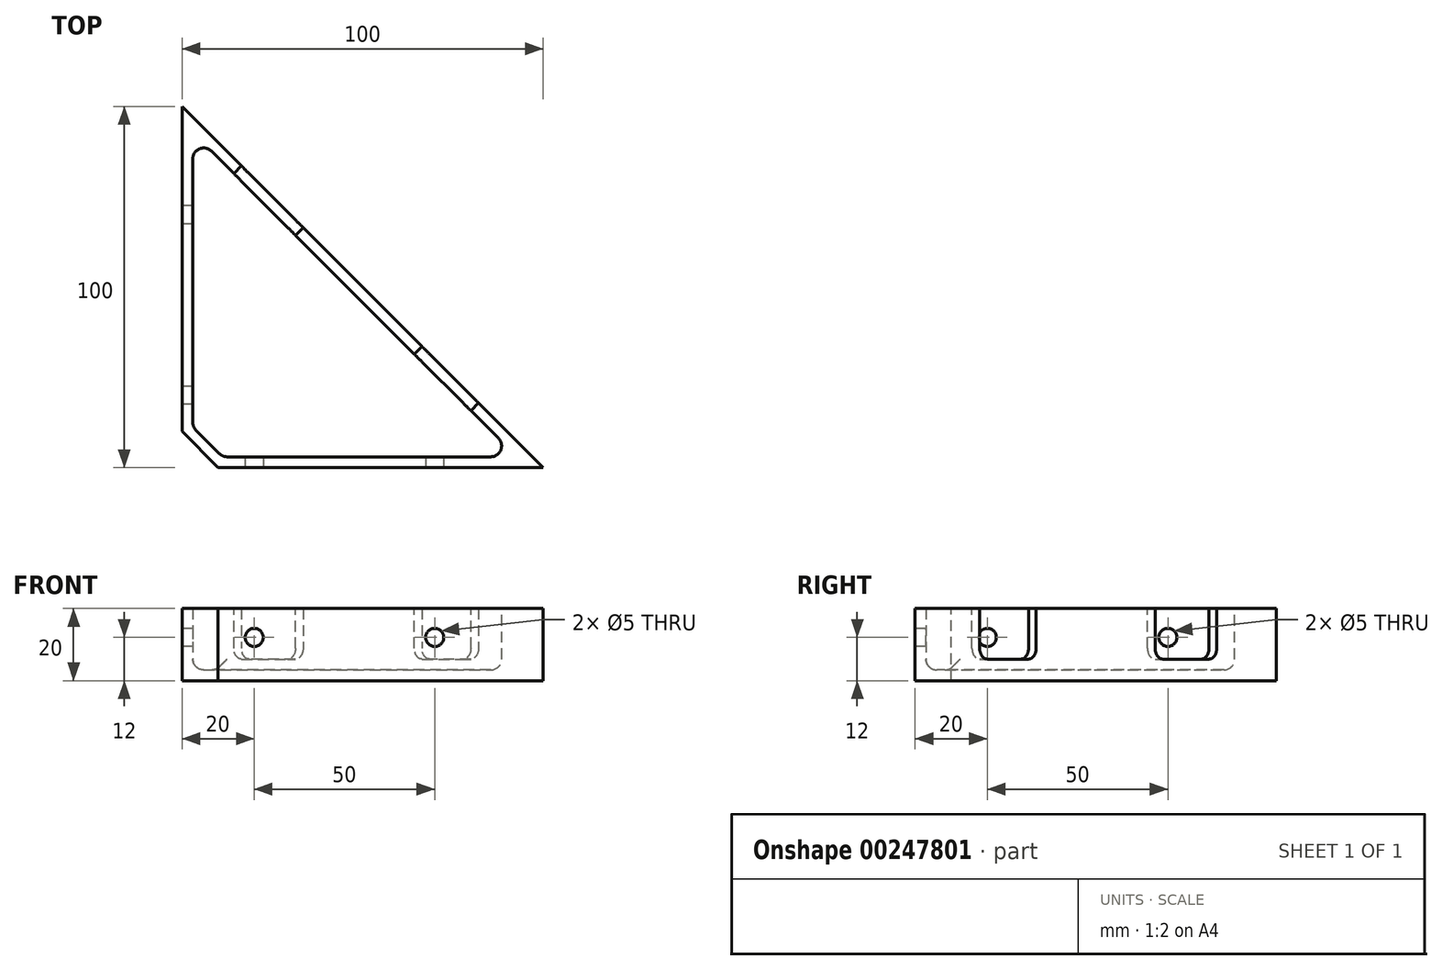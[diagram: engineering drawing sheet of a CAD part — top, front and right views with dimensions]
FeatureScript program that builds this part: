
annotation { "Feature Type Name" : "Feature", "Feature Type Description" : "" }
export const myFeature = defineFeature(function(context is Context, id is Id, definition is map)
    precondition{}
    {
        {
            var Q0;
            Q0=qCreatedBy(makeId("Top.planeOp"),FACE);
            var sketch = newSketch(context, id + "F0", { "sketchPlane" : qUnion([Q0])});
            skLineSegment(sketch, "E0", {"start": v(0, 0) * mm, "end": v(0, 100) * mm});
            skLineSegment(sketch, "E1", {"start": v(0, 100) * mm, "end": v(100, 0) * mm});
            skLineSegment(sketch, "E2", {"start": v(100, 0) * mm, "end": v(0, 0) * mm});
            skLineSegment(sketch, "E3", {"start": v(0, 20) * mm, "end": v(91.8, 20) * mm, "construction": true});
            skLineSegment(sketch, "E4", {"start": v(0, 70) * mm, "end": v(91.8, 70) * mm, "construction": true});
            skLineSegment(sketch, "E5", {"start": v(20, 0) * mm, "end": v(20, 100.49) * mm, "construction": true});
            skLineSegment(sketch, "E6", {"start": v(70, 0) * mm, "end": v(70, 96.45) * mm, "construction": true});
            skSolve(sketch);
        }
        {
            var Q0;
            Q0 = qSketchRegion(id + "F0", true);
            extrude(context, id + "F1", {"entities" : qUnion([Q0]), "depth" : 20 * mm});
        }
        {
            var Q0;
            Q0=makeQuery(id+"F1.opExtrude","SWEPT_EDGE",EDGE,{"disambiguationData":[OSD([sQuery(id+"F0.wireOp",EDGE,"E0"),sQuery(id+"F0.wireOp",EDGE,"E2")])]});
            chamfer(context, id + "F2", {"entities" : qUnion([Q0]), "width" : 10 * mm, "tangentPropagation" : true});
        }
        {
            var Q0;
            Q0=makeQuery(id+"F1.opExtrude","CAP_FACE",FACE,{"disambiguationData":[OSD([sQuery(id+"F0.wireOp",EDGE,"E0"),sQuery(id+"F0.wireOp",EDGE,"E1"),sQuery(id+"F0.wireOp",EDGE,"E2")])],"isStart":false});
            shell(context, id + "F3", {"entities" : qUnion([Q0]), "thickness" : 3 * mm});
        }
        {
            var Q0;
            Q0=qCreatedBy(makeId("Right.planeOp"),FACE);
            var sketch = newSketch(context, id + "F4", { "sketchPlane" : qUnion([Q0])});
            skCircle(sketch, "E7", {"center": v(20, 12) * mm, "radius": 2.5 * mm});
            skCircle(sketch, "E8", {"center": v(70, 12) * mm, "radius": 2.5 * mm});
            skSolve(sketch);
        }
        {
            var Q0;
            Q0=qCreatedBy(makeId("Front.planeOp"),FACE);
            var sketch = newSketch(context, id + "F5", { "sketchPlane" : qUnion([Q0])});
            skCircle(sketch, "E9", {"center": v(20, 12) * mm, "radius": 2.5 * mm});
            skCircle(sketch, "E10", {"center": v(70, 12) * mm, "radius": 2.5 * mm});
            skSolve(sketch);
        }
        {
            var Q0;
            Q0 = qSketchRegion(id + "F5", true);
            extrude(context, id + "F6", {"entities" : qUnion([Q0]), "operationType" : NewBodyOperationType.REMOVE, "endBound" : BoundingType.UP_TO_NEXT, "oppositeDirection" : true, "depth" : 25 * mm});
        }
        {
            var Q0;
            Q0 = qSketchRegion(id + "F4", true);
            extrude(context, id + "F7", {"entities" : qUnion([Q0]), "operationType" : NewBodyOperationType.REMOVE, "endBound" : BoundingType.UP_TO_NEXT, "depth" : 25 * mm});
        }
        {
            var Q0;
            Q0=makeQuery(id+"F1.opExtrude","SWEPT_FACE",FACE,{"disambiguationData":[OSD([sQuery(id+"F0.wireOp",EDGE,"E1")])]});
            var sketch = newSketch(context, id + "F8", { "sketchPlane" : qUnion([Q0])});
            skLineSegment(sketch, "E11.bottom", {"start": v(-45.43, 20) * mm, "end": v(-23.28, 20) * mm});
            skLineSegment(sketch, "E11.top", {"start": v(-42.43, 6) * mm, "end": v(-26.28, 6) * mm});
            skLineSegment(sketch, "E11.left", {"start": v(-45.43, 20) * mm, "end": v(-45.43, 9) * mm});
            skLineSegment(sketch, "E11.right", {"start": v(-23.28, 20) * mm, "end": v(-23.28, 9) * mm});
            skLineSegment(sketch, "E12.bottom", {"start": v(23.28, 20) * mm, "end": v(47.43, 20) * mm});
            skLineSegment(sketch, "E12.top", {"start": v(26.28, 6) * mm, "end": v(44.43, 6) * mm});
            skLineSegment(sketch, "E12.left", {"start": v(23.28, 20) * mm, "end": v(23.28, 9) * mm});
            skLineSegment(sketch, "E12.right", {"start": v(47.43, 20) * mm, "end": v(47.43, 9) * mm});
            skPoint(sketch, "E13", {"position": v(28.28, 0) * mm});
            skPoint(sketch, "E14", {"position": v(42.43, 0) * mm});
            skPoint(sketch, "E15", {"position": v(-42.43, 0) * mm});
            skPoint(sketch, "E16", {"position": v(-28.28, 0) * mm});
            skPoint(sketch, "E17.visualSharp", {"position": v(-45.43, 6) * mm});
            skArc(sketch, "E17.filletArc", {"start": v(-45.43, 9) * mm, "mid": v(-44.55, 6.88) * mm, "end": v(-42.43, 6) * mm});
            skPoint(sketch, "E18.visualSharp", {"position": v(-23.28, 6) * mm});
            skArc(sketch, "E18.filletArc", {"start": v(-26.28, 6) * mm, "mid": v(-24.16, 6.88) * mm, "end": v(-23.28, 9) * mm});
            skPoint(sketch, "E19.visualSharp", {"position": v(23.28, 6) * mm});
            skArc(sketch, "E19.filletArc", {"start": v(23.28, 9) * mm, "mid": v(24.16, 6.88) * mm, "end": v(26.28, 6) * mm});
            skPoint(sketch, "E20.visualSharp", {"position": v(47.43, 6) * mm});
            skArc(sketch, "E20.filletArc", {"start": v(44.43, 6) * mm, "mid": v(46.55, 6.88) * mm, "end": v(47.43, 9) * mm});
            skSolve(sketch);
        }
        {
            var Q0;
            Q0=makeQuery(id+"F3.opShell","OFFSET_EDGE",EDGE,{"disambiguationData":[OSD([sQuery(id+"F0.wireOp",EDGE,"E0"),sQuery(id+"F0.wireOp",EDGE,"E2")])]});
            var Q1;
            Q1=makeQuery(id+"F3.opShell","OFFSET_EDGE",EDGE,{"disambiguationData":[OSD([sQuery(id+"F0.wireOp",EDGE,"E1"),sQuery(id+"F0.wireOp",EDGE,"E2")])]});
            var Q2;
            Q2=makeQuery(id+"F3.opShell","OFFSET_EDGE",EDGE,{"disambiguationData":[OSD([sQuery(id+"F0.wireOp",EDGE,"E0"),sQuery(id+"F0.wireOp",EDGE,"E1")])]});
            var Q3;
            {var subQ0=sQuery(id+"F0.wireOp",EDGE,"E0");Q3=makeQuery(id+"F3.opShell","OFFSET_EDGE",EDGE,{"disambiguationData":[OSD([subQ0]),TDD([makeQuery(id+"F1.opExtrude","CAP_EDGE",EDGE,{"disambiguationData":[OSD([subQ0])],"isStart":true})])]});}
            var Q4;
            {var subQ0=sQuery(id+"F0.wireOp",EDGE,"E1");Q4=makeQuery(id+"F3.opShell","OFFSET_EDGE",EDGE,{"disambiguationData":[OSD([subQ0]),TDD([makeQuery(id+"F1.opExtrude","CAP_EDGE",EDGE,{"disambiguationData":[OSD([subQ0])],"isStart":true})])]});}
            var Q5;
            {var subQ0=sQuery(id+"F0.wireOp",EDGE,"E2");Q5=makeQuery(id+"F3.opShell","OFFSET_EDGE",EDGE,{"disambiguationData":[OSD([subQ0]),TDD([makeQuery(id+"F1.opExtrude","CAP_EDGE",EDGE,{"disambiguationData":[OSD([subQ0])],"isStart":true})])]});}
            fillet(context, id + "F9", {"entities" : qUnion([Q0, Q1, Q2, Q3, Q4, Q5]), "radius" : 3 * mm, "tangentPropagation" : true, "allowEdgeOverflow" : false});
        }
        {
            var Q0;
            Q0 = qSketchRegion(id + "F8", true);
            extrude(context, id + "F10", {"entities" : qUnion([Q0]), "operationType" : NewBodyOperationType.REMOVE, "endBound" : BoundingType.UP_TO_NEXT, "oppositeDirection" : true, "depth" : 25 * mm});
        }
    });
